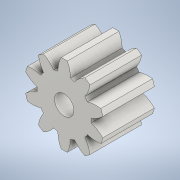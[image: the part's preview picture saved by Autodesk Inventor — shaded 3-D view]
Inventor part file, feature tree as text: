
AUTODESK INVENTOR PART (.ipt)
format: ipt  version: 2021 (Build 250183000, 183)  size: 202,752 bytes
history: native  units: mm (DEFAULTED — no unit token found)
features: plane x3, other x3, sketch x3, extrude x1, hole x1
ambient origin geometry x8: Origin, YZ Plane, XZ Plane, XY Plane, X Axis, Y Axis, Z Axis, Center Point
bodies: Solid1 (feature_tree)
feature tree (11):
  extrude  "Extrusion1"  Depth=8.0mm TaperAngle=0.0deg
  plane  "Work Plane2"
  plane  "Work Plane8"
  plane  "Work Plane9"
  other  "Spur Gear"
  hole  "Hole1"  [1 undecoded]
  sketch  "Sketch1"  dims[d0=12.303391mm d1=8.0mm d2=0.0mm]
  sketch  "Sketch2"  dims[d3=10.0mm d4=10.0mm d5=0.0mm]
  other  "Srf1"
  sketch  "Sketch3"  dims[d16=25.351695mm d17=0.0mm d34=3.141593mm d39=0.0mm d41=0.0mm d43=25.351695mm d46=25.351695mm d47=0.0mm d48=0.0mm d49=3.0mm d50=3.0mm d51=6.0mm d52=4.0mm d53=2.0mm d54=90.0deg d55=8.0mm d56=20.594885mm]
  other  "Pitch Diameter"
note: 1 required parameter value undecoded (feature->parameter linkage not recoverable at this tier; creation-order binding heuristic only, values carry confidence <= 0.55)
